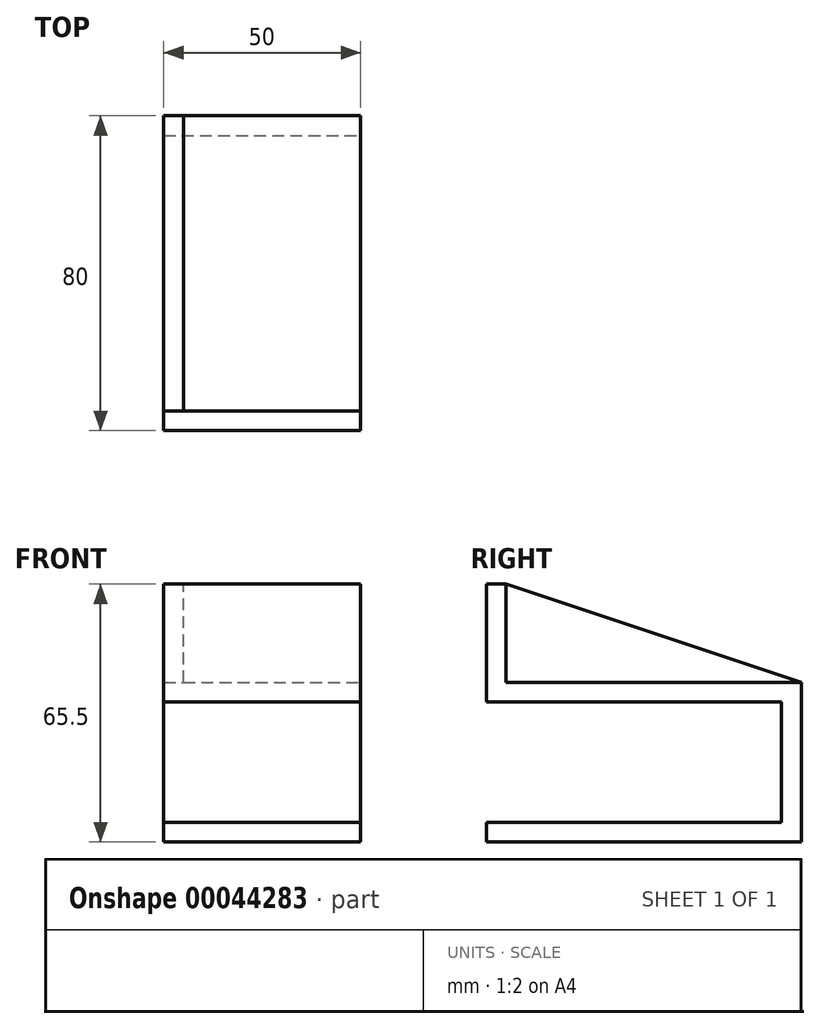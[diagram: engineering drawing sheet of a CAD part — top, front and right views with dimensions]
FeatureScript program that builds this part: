
annotation { "Feature Type Name" : "Feature", "Feature Type Description" : "" }
export const myFeature = defineFeature(function(context is Context, id is Id, definition is map)
    precondition{}
    {
        {
            var Q0;
            Q0=qCreatedBy(makeId("Top.planeOp"),FACE);
            var sketch = newSketch(context, id + "F0", { "sketchPlane" : qUnion([Q0])});
            skLineSegment(sketch, "E0.bottom", {"start": v(-25, 2.5) * mm, "end": v(25, 2.5) * mm});
            skLineSegment(sketch, "E0.top", {"start": v(-25, -2.5) * mm, "end": v(25, -2.5) * mm});
            skLineSegment(sketch, "E0.left", {"start": v(-25, 2.5) * mm, "end": v(-25, -2.5) * mm});
            skLineSegment(sketch, "E0.right", {"start": v(25, 2.5) * mm, "end": v(25, -2.5) * mm});
            skLineSegment(sketch, "E1", {"start": v(0, -2.5) * mm, "end": v(0, 2.5) * mm});
            skLineSegment(sketch, "E2", {"start": v(-25, 0) * mm, "end": v(25, 0) * mm});
            skSolve(sketch);
        }
        {
            var Q0;
            Q0 = qSketchRegion(id + "F0", true);
            extrude(context, id + "F1", {"entities" : qUnion([Q0]), "depth" : 30.5 * mm});
        }
        {
            var Q0;
            Q0=makeQuery(id+"F1.opExtrude","CAP_FACE",FACE,{"disambiguationData":[OSD([sQuery(id+"F0.wireOp",EDGE,"E0.bottom"),sQuery(id+"F0.wireOp",EDGE,"E0.top"),sQuery(id+"F0.wireOp",EDGE,"E0.left"),sQuery(id+"F0.wireOp",EDGE,"E0.right")])],"isStart":false});
            var sketch = newSketch(context, id + "F2", { "sketchPlane" : qUnion([Q0])});
            skLineSegment(sketch, "E3.bottom", {"start": v(-25, 2.5) * mm, "end": v(25, 2.5) * mm});
            skLineSegment(sketch, "E3.top", {"start": v(-25, -77.5) * mm, "end": v(25, -77.5) * mm});
            skLineSegment(sketch, "E3.left", {"start": v(-25, 2.5) * mm, "end": v(-25, -77.5) * mm});
            skLineSegment(sketch, "E3.right", {"start": v(25, 2.5) * mm, "end": v(25, -77.5) * mm});
            skSolve(sketch);
        }
        {
            var Q0;
            Q0 = qSketchRegion(id + "F2", true);
            extrude(context, id + "F3", {"entities" : qUnion([Q0]), "operationType" : NewBodyOperationType.ADD, "depth" : 5 * mm});
        }
        {
            var Q0;
            Q0=makeQuery(id+"F3.opExtrude","CAP_FACE",FACE,{"disambiguationData":[OSD([sQuery(id+"F2.wireOp",EDGE,"E3.bottom"),sQuery(id+"F2.wireOp",EDGE,"E3.top"),sQuery(id+"F2.wireOp",EDGE,"E3.left"),sQuery(id+"F2.wireOp",EDGE,"E3.right")])],"isStart":false});
            var sketch = newSketch(context, id + "F4", { "sketchPlane" : qUnion([Q0])});
            skLineSegment(sketch, "E4.bottom", {"start": v(-25, -77.5) * mm, "end": v(25, -77.5) * mm});
            skLineSegment(sketch, "E4.top", {"start": v(-25, -72.5) * mm, "end": v(25, -72.5) * mm});
            skLineSegment(sketch, "E4.left", {"start": v(-25, -77.5) * mm, "end": v(-25, -72.5) * mm});
            skLineSegment(sketch, "E4.right", {"start": v(25, -77.5) * mm, "end": v(25, -72.5) * mm});
            skSolve(sketch);
        }
        {
            var Q0;
            Q0 = qSketchRegion(id + "F4", true);
            extrude(context, id + "F5", {"entities" : qUnion([Q0]), "operationType" : NewBodyOperationType.ADD, "depth" : 25 * mm});
        }
        {
            var Q0;
            Q0=makeQuery(id+"F5.boolean.opBoolean","MERGE",FACE,{"derivedFrom":[makeQuery(id+"F3.boolean.opBoolean","MERGE",FACE,{"derivedFrom":[makeQuery(id+"F1.opExtrude","SWEPT_FACE",FACE,{"disambiguationData":[OSD([sQuery(id+"F0.wireOp",EDGE,"E0.left")])]}),makeQuery(id+"F3.opExtrude","SWEPT_FACE",FACE,{"disambiguationData":[OSD([sQuery(id+"F2.wireOp",EDGE,"E3.left")])]})]}),makeQuery(id+"F5.opExtrude","SWEPT_FACE",FACE,{"disambiguationData":[OSD([sQuery(id+"F4.wireOp",EDGE,"E4.left")])]})]});
            var sketch = newSketch(context, id + "F6", { "sketchPlane" : qUnion([Q0])});
            skLineSegment(sketch, "E5", {"start": v(77.5, 60.5) * mm, "end": v(72.5, 60.5) * mm});
            skLineSegment(sketch, "E6", {"start": v(72.5, 60.5) * mm, "end": v(-2.5, 35.5) * mm});
            skLineSegment(sketch, "E7", {"start": v(-2.5, 35.5) * mm, "end": v(77.5, 30.5) * mm});
            skLineSegment(sketch, "E8", {"start": v(77.5, 30.5) * mm, "end": v(77.5, 60.5) * mm});
            skSolve(sketch);
        }
        {
            var Q0;
            Q0 = qSketchRegion(id + "F6", true);
            extrude(context, id + "F7", {"entities" : qUnion([Q0]), "operationType" : NewBodyOperationType.ADD, "oppositeDirection" : true, "depth" : 5 * mm});
        }
        {
            var Q0;
            Q0=makeQuery(id+"F3.boolean.opBoolean","MERGE",FACE,{"derivedFrom":[makeQuery(id+"F1.opExtrude","SWEPT_FACE",FACE,{"disambiguationData":[OSD([sQuery(id+"F0.wireOp",EDGE,"E0.bottom")])]}),makeQuery(id+"F3.opExtrude","SWEPT_FACE",FACE,{"disambiguationData":[OSD([sQuery(id+"F2.wireOp",EDGE,"E3.bottom")])]})]});
            var sketch = newSketch(context, id + "F8", { "sketchPlane" : qUnion([Q0])});
            skLineSegment(sketch, "E9.bottom", {"start": v(-25, 0) * mm, "end": v(25, 0) * mm});
            skLineSegment(sketch, "E9.top", {"start": v(-25, -5) * mm, "end": v(25, -5) * mm});
            skLineSegment(sketch, "E9.left", {"start": v(-25, 0) * mm, "end": v(-25, -5) * mm});
            skLineSegment(sketch, "E9.right", {"start": v(25, 0) * mm, "end": v(25, -5) * mm});
            skSolve(sketch);
        }
        {
            var Q0;
            Q0 = qSketchRegion(id + "F8", true);
            var Q1;
            Q1=makeQuery(id+"F5.boolean.opBoolean","MERGE",FACE,{"derivedFrom":[makeQuery(id+"F3.opExtrude","SWEPT_FACE",FACE,{"disambiguationData":[OSD([sQuery(id+"F2.wireOp",EDGE,"E3.top")])]}),makeQuery(id+"F5.opExtrude","SWEPT_FACE",FACE,{"disambiguationData":[OSD([sQuery(id+"F4.wireOp",EDGE,"E4.bottom")])]})]});
            extrude(context, id + "F9", {"entities" : qUnion([Q0]), "operationType" : NewBodyOperationType.ADD, "endBound" : BoundingType.UP_TO_SURFACE, "oppositeDirection" : true, "endBoundEntityFace" : qUnion([Q1]), "depth" : 25 * mm});
        }
    });
